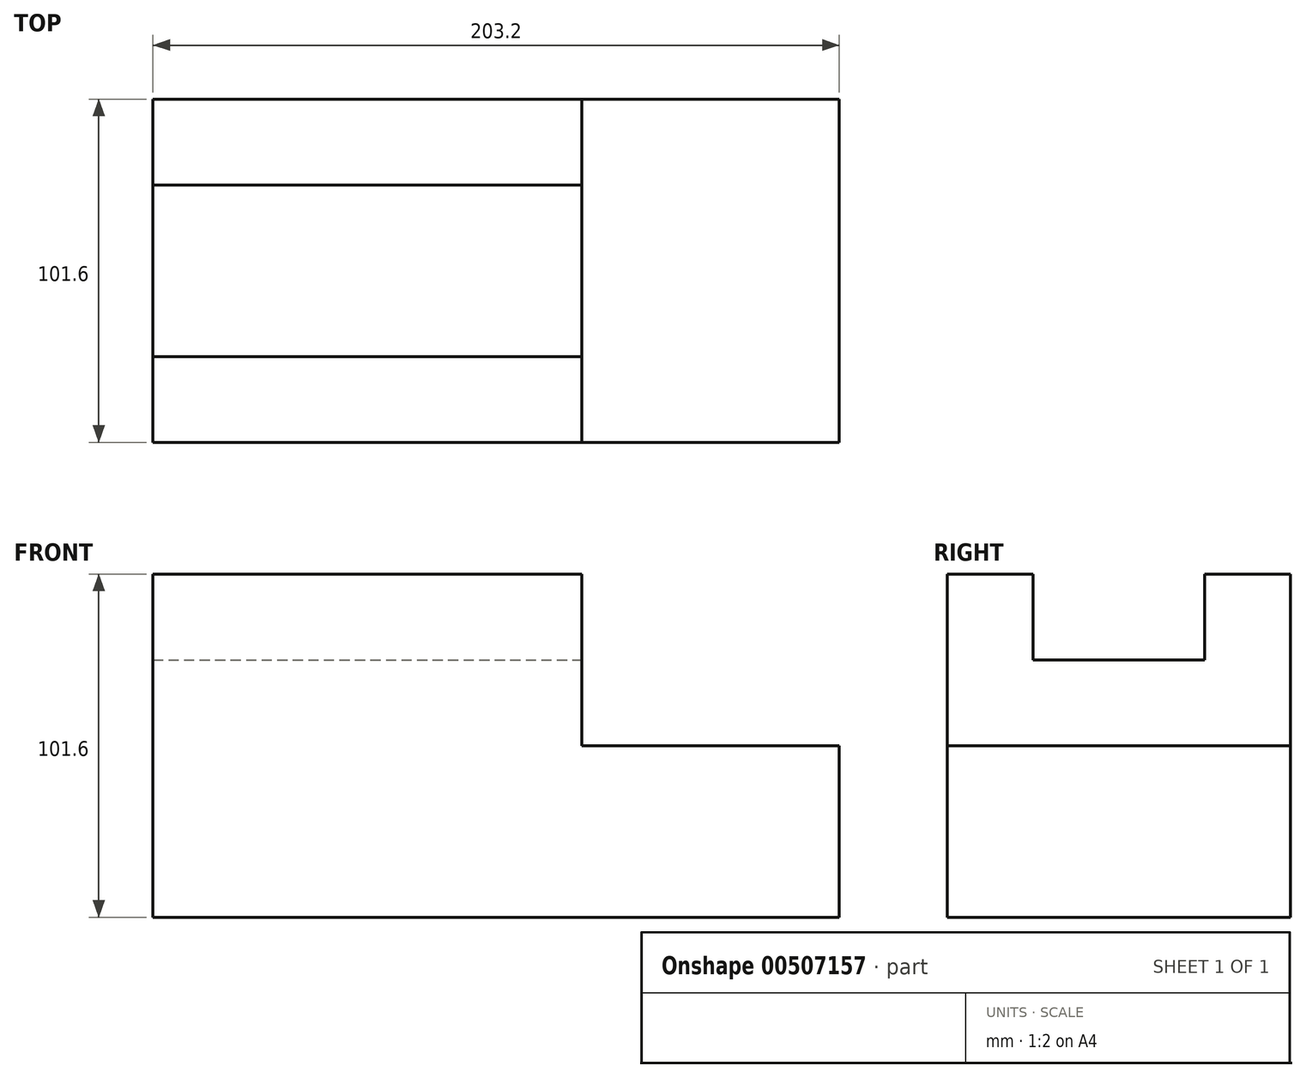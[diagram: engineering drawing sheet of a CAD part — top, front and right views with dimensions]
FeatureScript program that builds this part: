
annotation { "Feature Type Name" : "Feature", "Feature Type Description" : "" }
export const myFeature = defineFeature(function(context is Context, id is Id, definition is map)
    precondition{}
    {
        {
            var Q0;
            Q0=qCreatedBy(makeId("Front.planeOp"),FACE);
            var sketch = newSketch(context, id + "F0", { "sketchPlane" : qUnion([Q0])});
            skLineSegment(sketch, "E0", {"start": v(-67.63, 43.63) * mm, "end": v(-67.63, -57.97) * mm});
            skLineSegment(sketch, "E1", {"start": v(-67.63, -57.97) * mm, "end": v(135.57, -57.97) * mm});
            skLineSegment(sketch, "E2", {"start": v(135.57, -57.97) * mm, "end": v(135.57, -7.17) * mm});
            skLineSegment(sketch, "E3", {"start": v(135.57, -7.17) * mm, "end": v(59.37, -7.17) * mm});
            skLineSegment(sketch, "E4", {"start": v(59.37, -7.17) * mm, "end": v(59.37, 43.63) * mm});
            skLineSegment(sketch, "E5", {"start": v(59.37, 43.63) * mm, "end": v(-67.63, 43.63) * mm});
            skSolve(sketch);
        }
        {
            var Q0;
            Q0 = qSketchRegion(id + "F0", true);
            extrude(context, id + "F1", {"entities" : qUnion([Q0]), "depth" : 101.6 * mm});
        }
        {
            var Q0;
            Q0=makeQuery(id+"F1.opExtrude","SWEPT_FACE",FACE,{"disambiguationData":[OSD([sQuery(id+"F0.wireOp",EDGE,"E5")])]});
            var sketch = newSketch(context, id + "F2", { "sketchPlane" : qUnion([Q0])});
            skSolve(sketch);
        }
        {
            var Q0;
            {var subQ0=sQuery(id+"F0.wireOp",EDGE,"E5");Q0=makeQuery(id+"F2.imprint","IMPRINT",FACE,{"disambiguationData":[TD([[makeQuery(id+"F2.imprint","IMPRINT",EDGE,{"derivedFrom":makeQuery(id+"F1.opExtrude","CAP_EDGE",EDGE,{"disambiguationData":[OSD([subQ0])],"isStart":true})}),1.0]])]});}
            var sketch = newSketch(context, id + "F3", { "sketchPlane" : qUnion([Q0])});
            skLineSegment(sketch, "E6", {"start": v(-67.63, -25.4) * mm, "end": v(59.37, -25.4) * mm});
            skLineSegment(sketch, "E7", {"start": v(59.37, -76.2) * mm, "end": v(59.37, -25.4) * mm});
            skLineSegment(sketch, "E8", {"start": v(59.37, -76.2) * mm, "end": v(-67.63, -76.2) * mm});
            skLineSegment(sketch, "E9", {"start": v(-67.63, -76.2) * mm, "end": v(-67.63, -25.4) * mm});
            skSolve(sketch);
        }
        {
            var Q0;
            Q0 = qSketchRegion(id + "F3", true);
            extrude(context, id + "F4", {"entities" : qUnion([Q0]), "operationType" : NewBodyOperationType.REMOVE, "oppositeDirection" : true, "depth" : 25.4 * mm});
        }
    });
